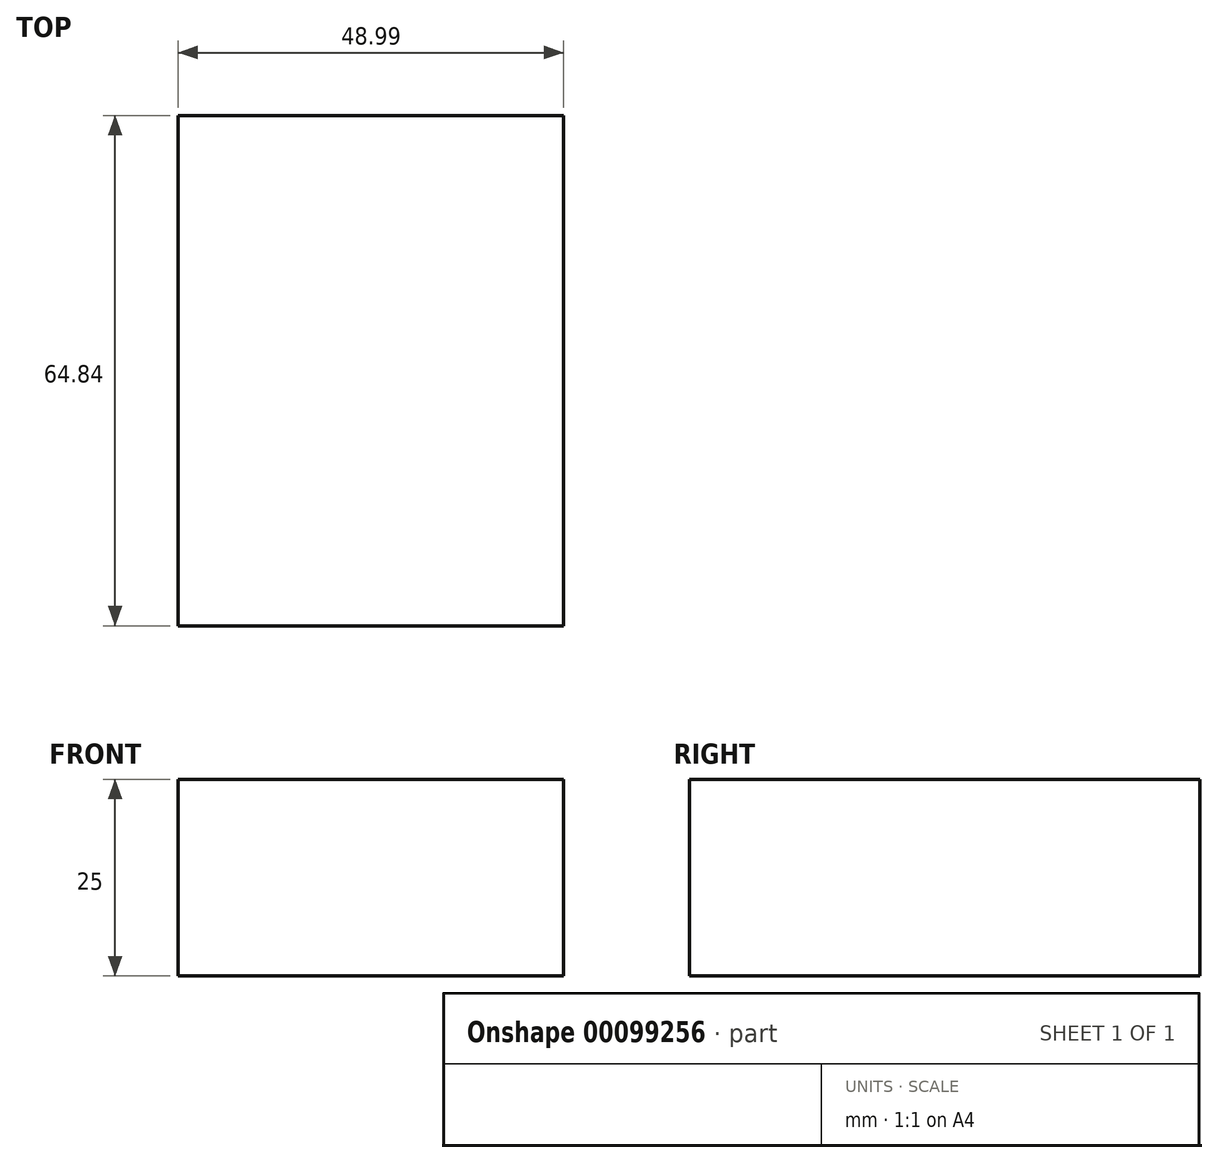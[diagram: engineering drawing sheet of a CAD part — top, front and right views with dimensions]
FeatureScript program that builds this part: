
annotation { "Feature Type Name" : "Feature", "Feature Type Description" : "" }
export const myFeature = defineFeature(function(context is Context, id is Id, definition is map)
    precondition{}
    {
        {
            var Q0;
            Q0=qCreatedBy(makeId("Top.planeOp"),FACE);
            var sketch = newSketch(context, id + "F0", { "sketchPlane" : qUnion([Q0])});
            skLineSegment(sketch, "E0.bottom", {"start": v(-34.05, -39.29) * mm, "end": v(14.94, -39.29) * mm});
            skLineSegment(sketch, "E0.top", {"start": v(-34.05, 25.55) * mm, "end": v(14.94, 25.55) * mm});
            skLineSegment(sketch, "E0.left", {"start": v(-34.05, -39.29) * mm, "end": v(-34.05, 25.55) * mm});
            skLineSegment(sketch, "E0.right", {"start": v(14.94, -39.29) * mm, "end": v(14.94, 25.55) * mm});
            skSolve(sketch);
        }
        {
            var Q0;
            Q0=makeQuery(id+"F0.imprint","IMPRINT",FACE,{"disambiguationData":[TD([[makeQuery(id+"F0.imprint","IMPRINT",EDGE,{"derivedFrom":sQuery(id+"F0.wireOp",EDGE,"E0.bottom")}),1.0]])]});
            extrude(context, id + "F1", {"entities" : qUnion([Q0]), "depth" : 25 * mm});
        }
    });
